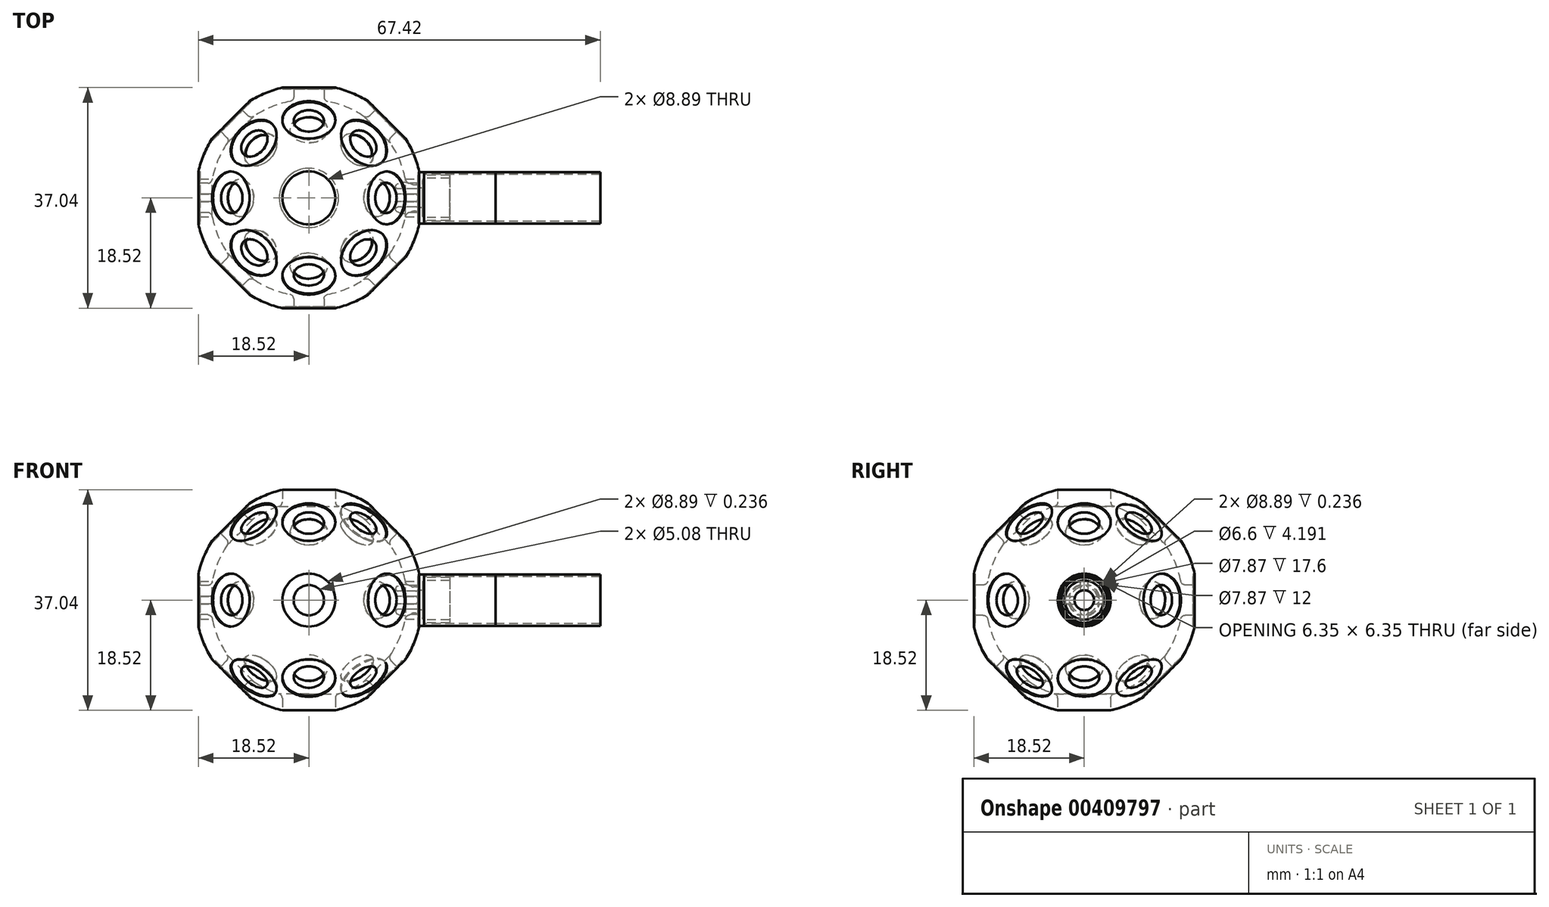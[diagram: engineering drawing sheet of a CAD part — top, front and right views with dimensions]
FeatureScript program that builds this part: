
annotation { "Feature Type Name" : "Feature", "Feature Type Description" : "" }
export const myFeature = defineFeature(function(context is Context, id is Id, definition is map)
    precondition{}
    {
        {
            var Q0;
            Q0=qCreatedBy(makeId("Top.planeOp"),FACE);
            var sketch = newSketch(context, id + "F0", { "sketchPlane" : qUnion([Q0])});
            skArc(sketch, "E0", {"start": v(0, -19.05) * mm, "mid": v(19.05, 0) * mm, "end": v(0, 19.05) * mm});
            skLineSegment(sketch, "E1", {"start": v(0, 19.05) * mm, "end": v(0, 16.51) * mm});
            skArc(sketch, "E2", {"start": v(0, -16.51) * mm, "mid": v(16.51, 0) * mm, "end": v(0, 16.51) * mm});
            skLineSegment(sketch, "E3.trimOffspring", {"start": v(0, -16.51) * mm, "end": v(0, -19.05) * mm});
            skSolve(sketch);
        }
        {
            var Q0;
            Q0=makeQuery(id+"F0.imprint","IMPRINT",FACE,{"disambiguationData":[TD([[makeQuery(id+"F0.imprint","IMPRINT",EDGE,{"derivedFrom":sQuery(id+"F0.wireOp",EDGE,"E0")}),1.0]])]});
            var Q1;
            Q1=sQuery(id+"F0.wireOp",EDGE,"E1");
            revolve(context, id + "F1", {"entities" : qUnion([Q0]), "axis" : qUnion([Q1]), "revolveType" : RevolveType.FULL});
        }
        {
            var Q0;
            Q0=qCreatedBy(makeId("Top.planeOp"),FACE);
            var sketch = newSketch(context, id + "F2", { "sketchPlane" : qUnion([Q0])});
            skCircle(sketch, "E4", {"center": v(0, 0) * mm, "radius": 4.45 * mm});
            skSolve(sketch);
        }
        {
            var Q0;
            Q0 = qSketchRegion(id + "F2", true);
            extrude(context, id + "F3", {"entities" : qUnion([Q0]), "depth" : 50.8 * mm, "symmetric" : true});
        }
        {
            var Q0;
            Q0=qCreatedBy(makeId("Top.planeOp"),FACE);
            var sketch = newSketch(context, id + "F4", { "sketchPlane" : qUnion([Q0])});
            skCircle(sketch, "E5", {"center": v(0, 0) * mm, "radius": 2.54 * mm});
            skCircle(sketch, "E6.0", {"center": v(0, 0) * mm, "radius": 4.45 * mm});
            skSolve(sketch);
        }
        {
            var Q0;
            Q0 = qSketchRegion(id + "F4", true);
            extrude(context, id + "F5", {"entities" : qUnion([Q0]), "operationType" : NewBodyOperationType.REMOVE, "depth" : 36.58 * mm, "symmetric" : true});
        }
        {
            var Q0;
            Q0=qCreatedBy(makeId("Top.planeOp"),FACE);
            var sketch = newSketch(context, id + "F6", { "sketchPlane" : qUnion([Q0])});
            skLineSegment(sketch, "E7", {"start": v(0, 0) * mm, "end": v(25.4, 0) * mm});
            skLineSegment(sketch, "E8", {"start": v(25.4, 0) * mm, "end": v(0, 0) * mm});
            skLineSegment(sketch, "E9", {"start": v(0, 0) * mm, "end": v(0, 25.4) * mm});
            skLineSegment(sketch, "E10", {"start": v(0, 0) * mm, "end": v(17.96, 17.96) * mm});
            skLineSegment(sketch, "E11", {"start": v(0, 0) * mm, "end": v(-17.96, 17.96) * mm});
            skSolve(sketch);
        }
        {
            var Q0;
            Q0=makeQuery(id+"F3.opExtrude","SWEPT_BODY",BODY,{"disambiguationData":[OSD([sQuery(id+"F2.wireOp",EDGE,"E4")])]});
            var Q1;
            Q1=sQuery(id+"F6.wireOp",EDGE,"E9");
            circularPattern(context, id + "F7", {"entities" : qUnion([Q0]), "axis" : qUnion([Q1]), "angle" : 135 * degree, "instanceCount" : 4, "equalSpace" : true});
        }
        {
            var Q0;
            Q0=makeQuery(id+"F3.opExtrude","SWEPT_BODY",BODY,{"disambiguationData":[OSD([sQuery(id+"F2.wireOp",EDGE,"E4")])]});
            var Q1;
            Q1=sQuery(id+"F6.wireOp",EDGE,"E8");
            circularPattern(context, id + "F8", {"entities" : qUnion([Q0]), "axis" : qUnion([Q1]), "angle" : 135 * degree, "instanceCount" : 4, "equalSpace" : true});
        }
        {
            var Q0;
            Q0=makeQuery(id+"F3.opExtrude","SWEPT_BODY",BODY,{"disambiguationData":[OSD([sQuery(id+"F2.wireOp",EDGE,"E4")])]});
            var Q1;
            Q1=sQuery(id+"F6.wireOp",EDGE,"E10");
            circularPattern(context, id + "F9", {"entities" : qUnion([Q0]), "axis" : qUnion([Q1]), "angle" : 135 * degree, "instanceCount" : 4, "equalSpace" : true});
        }
        {
            var Q0;
            Q0=makeQuery(id+"F3.opExtrude","SWEPT_BODY",BODY,{"disambiguationData":[OSD([sQuery(id+"F2.wireOp",EDGE,"E4")])]});
            var Q1;
            Q1=sQuery(id+"F6.wireOp",EDGE,"E11");
            circularPattern(context, id + "F10", {"entities" : qUnion([Q0]), "axis" : qUnion([Q1]), "angle" : 135 * degree, "instanceCount" : 4, "equalSpace" : true});
        }
        {
            var Q0;
            Q0=makeQuery(id+"F10.opPattern","COPY",BODY,{"derivedFrom":makeQuery(id+"F3.opExtrude","SWEPT_BODY",BODY,{"disambiguationData":[OSD([sQuery(id+"F2.wireOp",EDGE,"E4")])]}),"instanceName":"3"});
            var Q1;
            Q1=makeQuery(id+"F3.opExtrude","SWEPT_BODY",BODY,{"disambiguationData":[OSD([sQuery(id+"F2.wireOp",EDGE,"E4")])]});
            var Q2;
            Q2=makeQuery(id+"F7.opPattern","COPY",BODY,{"derivedFrom":makeQuery(id+"F3.opExtrude","SWEPT_BODY",BODY,{"disambiguationData":[OSD([sQuery(id+"F2.wireOp",EDGE,"E4")])]}),"instanceName":"1"});
            var Q3;
            Q3=makeQuery(id+"F7.opPattern","COPY",BODY,{"derivedFrom":makeQuery(id+"F3.opExtrude","SWEPT_BODY",BODY,{"disambiguationData":[OSD([sQuery(id+"F2.wireOp",EDGE,"E4")])]}),"instanceName":"2"});
            var Q4;
            Q4=makeQuery(id+"F7.opPattern","COPY",BODY,{"derivedFrom":makeQuery(id+"F3.opExtrude","SWEPT_BODY",BODY,{"disambiguationData":[OSD([sQuery(id+"F2.wireOp",EDGE,"E4")])]}),"instanceName":"3"});
            var Q5;
            Q5=makeQuery(id+"F8.opPattern","COPY",BODY,{"derivedFrom":makeQuery(id+"F3.opExtrude","SWEPT_BODY",BODY,{"disambiguationData":[OSD([sQuery(id+"F2.wireOp",EDGE,"E4")])]}),"instanceName":"1"});
            var Q6;
            Q6=makeQuery(id+"F8.opPattern","COPY",BODY,{"derivedFrom":makeQuery(id+"F3.opExtrude","SWEPT_BODY",BODY,{"disambiguationData":[OSD([sQuery(id+"F2.wireOp",EDGE,"E4")])]}),"instanceName":"2"});
            var Q7;
            Q7=makeQuery(id+"F8.opPattern","COPY",BODY,{"derivedFrom":makeQuery(id+"F3.opExtrude","SWEPT_BODY",BODY,{"disambiguationData":[OSD([sQuery(id+"F2.wireOp",EDGE,"E4")])]}),"instanceName":"3"});
            var Q8;
            Q8=makeQuery(id+"F9.opPattern","COPY",BODY,{"derivedFrom":makeQuery(id+"F3.opExtrude","SWEPT_BODY",BODY,{"disambiguationData":[OSD([sQuery(id+"F2.wireOp",EDGE,"E4")])]}),"instanceName":"1"});
            var Q9;
            Q9=makeQuery(id+"F9.opPattern","COPY",BODY,{"derivedFrom":makeQuery(id+"F3.opExtrude","SWEPT_BODY",BODY,{"disambiguationData":[OSD([sQuery(id+"F2.wireOp",EDGE,"E4")])]}),"instanceName":"2"});
            var Q10;
            Q10=makeQuery(id+"F9.opPattern","COPY",BODY,{"derivedFrom":makeQuery(id+"F3.opExtrude","SWEPT_BODY",BODY,{"disambiguationData":[OSD([sQuery(id+"F2.wireOp",EDGE,"E4")])]}),"instanceName":"3"});
            var Q11;
            Q11=makeQuery(id+"F10.opPattern","COPY",BODY,{"derivedFrom":makeQuery(id+"F3.opExtrude","SWEPT_BODY",BODY,{"disambiguationData":[OSD([sQuery(id+"F2.wireOp",EDGE,"E4")])]}),"instanceName":"1"});
            var Q12;
            Q12=makeQuery(id+"F10.opPattern","COPY",BODY,{"derivedFrom":makeQuery(id+"F3.opExtrude","SWEPT_BODY",BODY,{"disambiguationData":[OSD([sQuery(id+"F2.wireOp",EDGE,"E4")])]}),"instanceName":"2"});
            var Q13;
            Q13=makeQuery(id+"F1.opRevolve","SWEPT_BODY",BODY,{"disambiguationData":[OSD([sQuery(id+"F0.wireOp",EDGE,"E0"),sQuery(id+"F0.wireOp",EDGE,"E1")])]});
            booleanBodies(context, id + "F11", {"operationType" : BooleanOperationType.SUBTRACTION, "tools" : qUnion([Q0, Q1, Q2, Q3, Q4, Q5, Q6, Q7, Q8, Q9, Q10, Q11, Q12]), "targets" : qUnion([Q13])});
        }
        {
            var Q0;
            Q0=makeQuery(id+"F1.opRevolve","SWEPT_FACE",FACE,{"disambiguationData":[OSD([sQuery(id+"F0.wireOp",EDGE,"E2")])]});
            fillet(context, id + "F12", {"entities" : qUnion([Q0]), "radius" : 0.76 * mm, "tangentPropagation" : true, "allowEdgeOverflow" : false});
        }
        {
            var Q0;
            Q0=qCreatedBy(makeId("Top.planeOp"),FACE);
            var sketch = newSketch(context, id + "F13", { "sketchPlane" : qUnion([Q0])});
            skLineSegment(sketch, "E12.bottom", {"start": v(18.29, 4.32) * mm, "end": v(19.3, 4.32) * mm});
            skLineSegment(sketch, "E12.left", {"start": v(18.29, 4.32) * mm, "end": v(18.29, 2.54) * mm});
            skLineSegment(sketch, "E13", {"start": v(23.62, 3.81) * mm, "end": v(23.62, 3.3) * mm});
            skArc(sketch, "E14", {"start": v(17.22, 2.37) * mm, "mid": v(16, 2.67) * mm, "end": v(14.78, 2.37) * mm});
            skLineSegment(sketch, "E15", {"start": v(18.03, 2.29) * mm, "end": v(17.57, 2.29) * mm});
            skLineSegment(sketch, "E16", {"start": v(13.34, 0) * mm, "end": v(23.62, 0) * mm, "construction": true});
            skLineSegment(sketch, "E17", {"start": v(19.05, 1.65) * mm, "end": v(14.95, 1.65) * mm});
            skLineSegment(sketch, "E18", {"start": v(19.3, 4.32) * mm, "end": v(19.3, 3.81) * mm});
            skLineSegment(sketch, "E19", {"start": v(19.3, 3.81) * mm, "end": v(23.62, 3.81) * mm});
            skLineSegment(sketch, "E20", {"start": v(23.62, 3.3) * mm, "end": v(19.43, 3.3) * mm});
            skLineSegment(sketch, "E21", {"start": v(19.05, 2.92) * mm, "end": v(19.05, 1.65) * mm});
            skPoint(sketch, "E22.visualSharp", {"position": v(19.05, 3.3) * mm});
            skArc(sketch, "E22.filletArc", {"start": v(19.43, 3.3) * mm, "mid": v(19.16, 3.2) * mm, "end": v(19.05, 2.92) * mm});
            skPoint(sketch, "E23.visualSharp", {"position": v(17.38, 2.29) * mm});
            skArc(sketch, "E23.filletArc", {"start": v(17.22, 2.37) * mm, "mid": v(17.4, 2.3) * mm, "end": v(17.57, 2.29) * mm});
            skPoint(sketch, "E24.visualSharp", {"position": v(13.9, 1.65) * mm});
            skArc(sketch, "E24.filletArc", {"start": v(14.78, 2.37) * mm, "mid": v(14.58, 1.94) * mm, "end": v(14.95, 1.65) * mm});
            skPoint(sketch, "E25.visualSharp", {"position": v(18.29, 2.29) * mm});
            skArc(sketch, "E25.filletArc", {"start": v(18.03, 2.29) * mm, "mid": v(18.21, 2.36) * mm, "end": v(18.29, 2.54) * mm});
            skSolve(sketch);
        }
        {
            var Q0;
            Q0 = qSketchRegion(id + "F13", true);
            var Q1;
            Q1=sQuery(id+"F13.wireOp",EDGE,"E16");
            revolve(context, id + "F14", {"entities" : qUnion([Q0]), "axis" : qUnion([Q1]), "revolveType" : RevolveType.FULL});
        }
        {
            var Q0;
            Q0=makeQuery(id+"F14.opRevolve","SWEPT_FACE",FACE,{"disambiguationData":[OSD([sQuery(id+"F13.wireOp",EDGE,"E12.left")])]});
            var sketch = newSketch(context, id + "F15", { "sketchPlane" : qUnion([Q0])});
            skLineSegment(sketch, "E26.bottom", {"start": v(0.63, 3.17) * mm, "end": v(-0.63, 3.17) * mm});
            skLineSegment(sketch, "E26.top", {"start": v(0.63, -3.17) * mm, "end": v(-0.63, -3.17) * mm});
            skLineSegment(sketch, "E26.left", {"start": v(0.64, 3.17) * mm, "end": v(0.64, -3.17) * mm});
            skLineSegment(sketch, "E26.right", {"start": v(-0.63, 3.17) * mm, "end": v(-0.63, -3.17) * mm});
            skLineSegment(sketch, "E27.bottom", {"start": v(3.18, 0.63) * mm, "end": v(-3.17, 0.63) * mm});
            skLineSegment(sketch, "E27.top", {"start": v(3.18, -0.63) * mm, "end": v(-3.17, -0.63) * mm});
            skLineSegment(sketch, "E27.left", {"start": v(3.17, 0.63) * mm, "end": v(3.18, -0.63) * mm});
            skLineSegment(sketch, "E27.right", {"start": v(-3.17, 0.63) * mm, "end": v(-3.17, -0.63) * mm});
            skSolve(sketch);
        }
        {
            var Q0;
            Q0 = qSketchRegion(id + "F15", true);
            extrude(context, id + "F16", {"entities" : qUnion([Q0]), "operationType" : NewBodyOperationType.REMOVE, "endBound" : BoundingType.THROUGH_ALL, "depth" : 25.4 * mm});
        }
        {
            var Q0;
            {var subQ0=sQuery(id+"F15.wireOp",EDGE,"E27.bottom");Q0=makeQuery(id+"F16.boolean.opBoolean","COPY",EDGE,{"derivedFrom":makeQuery(id+"F16.opExtrude","CAP_EDGE",EDGE,{"disambiguationData":[OSD([subQ0]),TDD([makeQuery(id+"F15.imprint","IMPRINT",EDGE,{"disambiguationData":[TD([[makeQuery(id+"F15.imprint","INTERSECT",VERTEX,{"derivedFrom":[subQ0,sQuery(id+"F15.wireOp",EDGE,"E27.left")]}),-1.0]])],"derivedFrom":subQ0}),makeQuery(id+"F15.imprint","IMPRINT",EDGE,{"disambiguationData":[TD([[makeQuery(id+"F15.imprint","INTERSECT",VERTEX,{"derivedFrom":[sQuery(id+"F15.wireOp",EDGE,"E26.left"),subQ0]}),1.0]])],"derivedFrom":subQ0})])],"isStart":true})});}
            var Q1;
            {var subQ0=sQuery(id+"F15.wireOp",EDGE,"E27.top");Q1=makeQuery(id+"F16.boolean.opBoolean","COPY",EDGE,{"derivedFrom":makeQuery(id+"F16.opExtrude","CAP_EDGE",EDGE,{"disambiguationData":[OSD([subQ0]),TDD([makeQuery(id+"F15.imprint","IMPRINT",EDGE,{"disambiguationData":[TD([[makeQuery(id+"F15.imprint","INTERSECT",VERTEX,{"derivedFrom":[subQ0,sQuery(id+"F15.wireOp",EDGE,"E27.left")]}),-1.0]])],"derivedFrom":subQ0}),makeQuery(id+"F15.imprint","IMPRINT",EDGE,{"disambiguationData":[TD([[makeQuery(id+"F15.imprint","INTERSECT",VERTEX,{"derivedFrom":[sQuery(id+"F15.wireOp",EDGE,"E26.left"),subQ0]}),1.0]])],"derivedFrom":subQ0})])],"isStart":true})});}
            var Q2;
            {var subQ0=sQuery(id+"F15.wireOp",EDGE,"E26.left");Q2=makeQuery(id+"F16.boolean.opBoolean","COPY",EDGE,{"derivedFrom":makeQuery(id+"F16.opExtrude","CAP_EDGE",EDGE,{"disambiguationData":[OSD([subQ0]),TDD([makeQuery(id+"F15.imprint","IMPRINT",EDGE,{"disambiguationData":[TD([[makeQuery(id+"F15.imprint","INTERSECT",VERTEX,{"derivedFrom":[sQuery(id+"F15.wireOp",EDGE,"E26.bottom"),subQ0]}),-1.0]])],"derivedFrom":subQ0}),makeQuery(id+"F15.imprint","IMPRINT",EDGE,{"disambiguationData":[TD([[makeQuery(id+"F15.imprint","INTERSECT",VERTEX,{"derivedFrom":[subQ0,sQuery(id+"F15.wireOp",EDGE,"E27.bottom")]}),1.0]])],"derivedFrom":subQ0})])],"isStart":true})});}
            var Q3;
            {var subQ0=sQuery(id+"F15.wireOp",EDGE,"E26.right");Q3=makeQuery(id+"F16.boolean.opBoolean","COPY",EDGE,{"derivedFrom":makeQuery(id+"F16.opExtrude","CAP_EDGE",EDGE,{"disambiguationData":[OSD([subQ0]),TDD([makeQuery(id+"F15.imprint","IMPRINT",EDGE,{"disambiguationData":[TD([[makeQuery(id+"F15.imprint","INTERSECT",VERTEX,{"derivedFrom":[sQuery(id+"F15.wireOp",EDGE,"E26.bottom"),subQ0]}),-1.0]])],"derivedFrom":subQ0}),makeQuery(id+"F15.imprint","IMPRINT",EDGE,{"disambiguationData":[TD([[makeQuery(id+"F15.imprint","INTERSECT",VERTEX,{"derivedFrom":[subQ0,sQuery(id+"F15.wireOp",EDGE,"E27.bottom")]}),1.0]])],"derivedFrom":subQ0})])],"isStart":true})});}
            var Q4;
            {var subQ0=sQuery(id+"F15.wireOp",EDGE,"E27.bottom");Q4=makeQuery(id+"F16.boolean.opBoolean","COPY",EDGE,{"derivedFrom":makeQuery(id+"F16.opExtrude","CAP_EDGE",EDGE,{"disambiguationData":[OSD([subQ0]),TDD([makeQuery(id+"F15.imprint","IMPRINT",EDGE,{"disambiguationData":[TD([[makeQuery(id+"F15.imprint","INTERSECT",VERTEX,{"derivedFrom":[sQuery(id+"F15.wireOp",EDGE,"E26.right"),subQ0]}),-1.0]])],"derivedFrom":subQ0}),makeQuery(id+"F15.imprint","IMPRINT",EDGE,{"disambiguationData":[TD([[makeQuery(id+"F15.imprint","INTERSECT",VERTEX,{"derivedFrom":[subQ0,sQuery(id+"F15.wireOp",EDGE,"E27.right")]}),1.0]])],"derivedFrom":subQ0})])],"isStart":true})});}
            var Q5;
            {var subQ0=sQuery(id+"F15.wireOp",EDGE,"E27.top");Q5=makeQuery(id+"F16.boolean.opBoolean","COPY",EDGE,{"derivedFrom":makeQuery(id+"F16.opExtrude","CAP_EDGE",EDGE,{"disambiguationData":[OSD([subQ0]),TDD([makeQuery(id+"F15.imprint","IMPRINT",EDGE,{"disambiguationData":[TD([[makeQuery(id+"F15.imprint","INTERSECT",VERTEX,{"derivedFrom":[sQuery(id+"F15.wireOp",EDGE,"E26.right"),subQ0]}),-1.0]])],"derivedFrom":subQ0}),makeQuery(id+"F15.imprint","IMPRINT",EDGE,{"disambiguationData":[TD([[makeQuery(id+"F15.imprint","INTERSECT",VERTEX,{"derivedFrom":[subQ0,sQuery(id+"F15.wireOp",EDGE,"E27.right")]}),1.0]])],"derivedFrom":subQ0})])],"isStart":true})});}
            var Q6;
            {var subQ0=sQuery(id+"F15.wireOp",EDGE,"E26.right");Q6=makeQuery(id+"F16.boolean.opBoolean","COPY",EDGE,{"derivedFrom":makeQuery(id+"F16.opExtrude","CAP_EDGE",EDGE,{"disambiguationData":[OSD([subQ0]),TDD([makeQuery(id+"F15.imprint","IMPRINT",EDGE,{"disambiguationData":[TD([[makeQuery(id+"F15.imprint","INTERSECT",VERTEX,{"derivedFrom":[subQ0,sQuery(id+"F15.wireOp",EDGE,"E27.top")]}),-1.0]])],"derivedFrom":subQ0}),makeQuery(id+"F15.imprint","IMPRINT",EDGE,{"disambiguationData":[TD([[makeQuery(id+"F15.imprint","INTERSECT",VERTEX,{"derivedFrom":[sQuery(id+"F15.wireOp",EDGE,"E26.top"),subQ0]}),1.0]])],"derivedFrom":subQ0})])],"isStart":true})});}
            var Q7;
            {var subQ0=sQuery(id+"F15.wireOp",EDGE,"E26.left");Q7=makeQuery(id+"F16.boolean.opBoolean","COPY",EDGE,{"derivedFrom":makeQuery(id+"F16.opExtrude","CAP_EDGE",EDGE,{"disambiguationData":[OSD([subQ0]),TDD([makeQuery(id+"F15.imprint","IMPRINT",EDGE,{"disambiguationData":[TD([[makeQuery(id+"F15.imprint","INTERSECT",VERTEX,{"derivedFrom":[subQ0,sQuery(id+"F15.wireOp",EDGE,"E27.top")]}),-1.0]])],"derivedFrom":subQ0}),makeQuery(id+"F15.imprint","IMPRINT",EDGE,{"disambiguationData":[TD([[makeQuery(id+"F15.imprint","INTERSECT",VERTEX,{"derivedFrom":[sQuery(id+"F15.wireOp",EDGE,"E26.top"),subQ0]}),1.0]])],"derivedFrom":subQ0})])],"isStart":true})});}
            fillet(context, id + "F17", {"entities" : qUnion([Q0, Q1, Q2, Q3, Q4, Q5, Q6, Q7]), "radius" : 0.38 * mm, "tangentPropagation" : true, "allowEdgeOverflow" : false});
        }
        {
            var Q0;
            Q0=makeQuery(id+"F14.opRevolve","SWEPT_FACE",FACE,{"disambiguationData":[OSD([sQuery(id+"F13.wireOp",EDGE,"E18")])]});
            var sketch = newSketch(context, id + "F18", { "sketchPlane" : qUnion([Q0])});
            skCircle(sketch, "E28.0", {"center": v(0, 0) * mm, "radius": 4.32 * mm});
            skCircle(sketch, "E29", {"center": v(0, 0) * mm, "radius": 3.94 * mm});
            skSolve(sketch);
        }
        {
            assignVariable(context, id + "F19", {"name" : "L1", "anyValue" : 12});
        }
        {
            assignVariable(context, id + "F20", {"name" : "L2", "anyValue" : 1.41 * (getVariable(context, 'L1') + 1.52) - 1.52});
        }
        {
            var Q0;
            Q0 = qSketchRegion(id + "F18", true);
            extrude(context, id + "F21", {"entities" : qUnion([Q0]), "depth" : (getVariable(context, 'L1')) * mm});
        }
        {
            var Q0;
            Q0=makeQuery(id+"F21.opExtrude","CAP_FACE",FACE,{"disambiguationData":[OSD([sQuery(id+"F18.wireOp",EDGE,"E28.0"),sQuery(id+"F18.wireOp",EDGE,"E29")])],"isStart":false});
            var sketch = newSketch(context, id + "F22", { "sketchPlane" : qUnion([Q0])});
            skCircle(sketch, "E30", {"center": v(0, 0) * mm, "radius": 3.94 * mm});
            skCircle(sketch, "E31", {"center": v(0, 0) * mm, "radius": 4.32 * mm});
            skSolve(sketch);
        }
        {
            var Q0;
            Q0 = qSketchRegion(id + "F22", true);
            extrude(context, id + "F23", {"entities" : qUnion([Q0]), "depth" : (getVariable(context, 'L2')) * mm});
        }
    });
